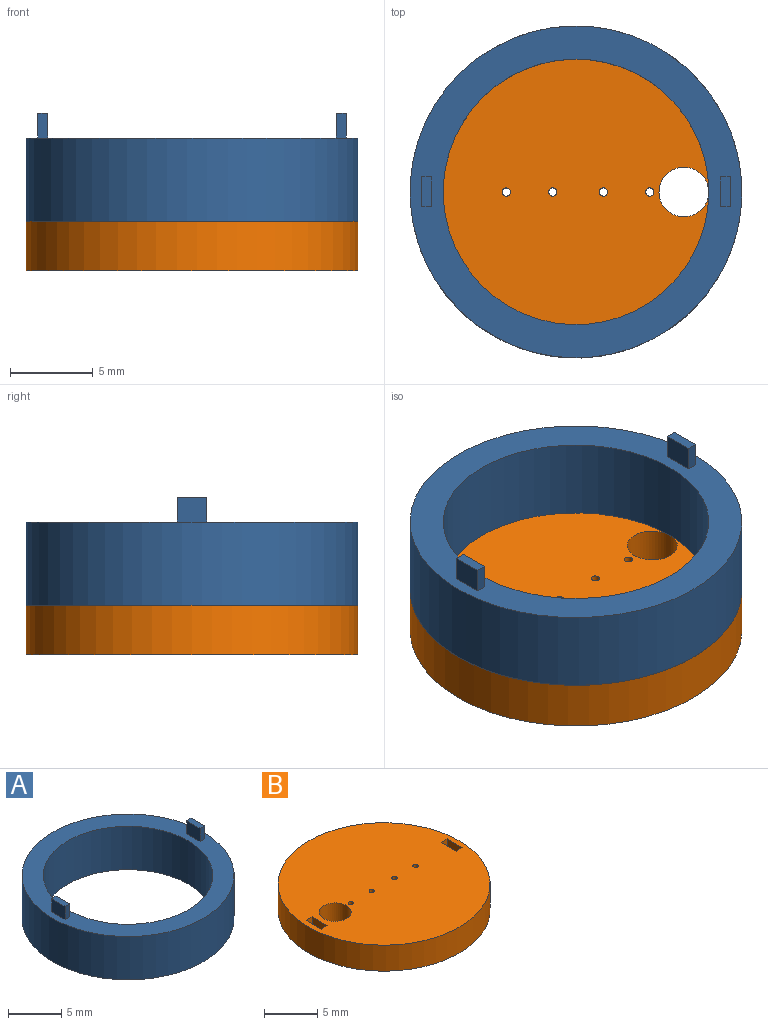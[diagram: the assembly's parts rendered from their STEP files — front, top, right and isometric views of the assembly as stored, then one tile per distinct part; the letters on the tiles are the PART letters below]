
ASSEMBLY  parts=2 mates=1
PART A: 14 faces, bbox 20x20x6.5 mm
  f0: plane 1.8x1.5mm, normal (-1,0,0), area 2.7mm2, adj f1,f3,f4,f12
  f1: plane 1.5x0.6mm, normal (0,-1,0), area 0.9mm2, adj f0,f2,f4,f12
  f2: plane 1.8x1.5mm, normal (1,0,0), area 2.7mm2, adj f1,f3,f4,f12
  f3: plane 1.5x0.6mm, normal (0,1,0), area 0.9mm2, adj f0,f2,f4,f12
  f4: plane 1.8x0.6mm, normal (0,0,1), area 1.1mm2, adj f0,f1,f2,f3
  f5: plane 1.8x1.5mm, normal (-1,0,0), area 2.7mm2, adj f6,f8,f9,f12
  f6: plane 1.5x0.6mm, normal (0,-1,0), area 0.9mm2, adj f5,f7,f9,f12
  f7: plane 1.8x1.5mm, normal (1,0,0), area 2.7mm2, adj f6,f8,f9,f12
  f8: plane 1.5x0.6mm, normal (0,1,0), area 0.9mm2, adj f5,f7,f9,f12
  f9: plane 1.8x0.6mm, normal (0,0,1), area 1.1mm2, adj f5,f6,f7,f8
  f10: cylinder r=8mm len=16mm, axis (0,0,-1), area 251.3mm2, adj f12,f13
  f11: cylinder r=10mm len=20mm, axis (0,0,-1), area 314.2mm2, adj f12,f13
  f12: plane 20x20mm, normal (0,0,1), area 110.9mm2, adj f0,f1,f2,f3,f5,f6,f7,f8
  f13: plane 20x20mm, normal (0,0,-1), area 113.1mm2, adj f10,f11
PART B: 18 faces, bbox 20x20x3 mm
  f0: plane 20x20mm, normal (0,0,-1), area 306.3mm2, adj f9,f10,f11,f12,f13,f14
  f1: plane 1.5x0.8mm, normal (0,-1,0), area 1.2mm2, adj f2,f4,f15,f17
  f2: plane 2x1.5mm, normal (1,0,0), area 3mm2, adj f1,f3,f15,f17
  f3: plane 1.5x0.8mm, normal (0,1,0), area 1.2mm2, adj f2,f4,f15,f17
  f4: plane 2x1.5mm, normal (-1,0,0), area 3mm2, adj f1,f3,f15,f17
  f5: plane 1.5x0.8mm, normal (0,-1,0), area 1.2mm2, adj f6,f8,f15,f16
  f6: plane 2x1.5mm, normal (1,0,0), area 3mm2, adj f5,f7,f15,f16
  f7: plane 1.5x0.8mm, normal (0,1,0), area 1.2mm2, adj f6,f8,f15,f16
  f8: plane 2x1.5mm, normal (-1,0,0), area 3mm2, adj f5,f7,f15,f16
  f9: cylinder r=0.25mm len=3mm, axis (0,0,-1), area 4.7mm2, adj f0,f15
  f10: cylinder r=0.25mm len=3mm, axis (0,0,-1), area 4.7mm2, adj f0,f15
  f11: cylinder r=1.5mm len=3mm, axis (0,0,-1), area 28.3mm2, adj f0,f15
  f12: cylinder r=0.25mm len=3mm, axis (0,0,-1), area 4.7mm2, adj f0,f15
  f13: cylinder r=0.25mm len=3mm, axis (0,0,-1), area 4.7mm2, adj f0,f15
  f14: cylinder r=10mm len=20mm, axis (0,0,-1), area 188.5mm2, adj f0,f15
  f15: plane 20x20mm, normal (0,0,1), area 303.1mm2, adj f1,f2,f3,f4,f5,f6,f7,f8
  f16: plane 2x0.8mm, normal (0,0,1), area 1.6mm2, adj f5,f6,f7,f8
  f17: plane 2x0.8mm, normal (0,0,1), area 1.6mm2, adj f1,f2,f3,f4
PLACE A t=(-0.66,9.58,2.03)mm
PLACE B rot(axis=(0,1,0),180deg) t=(-0.66,9.58,0.53)mm
MATE fastened B.f14 <-> A.f10  axis (0,0,1) through (-0.66,9.58,2.03)mm
